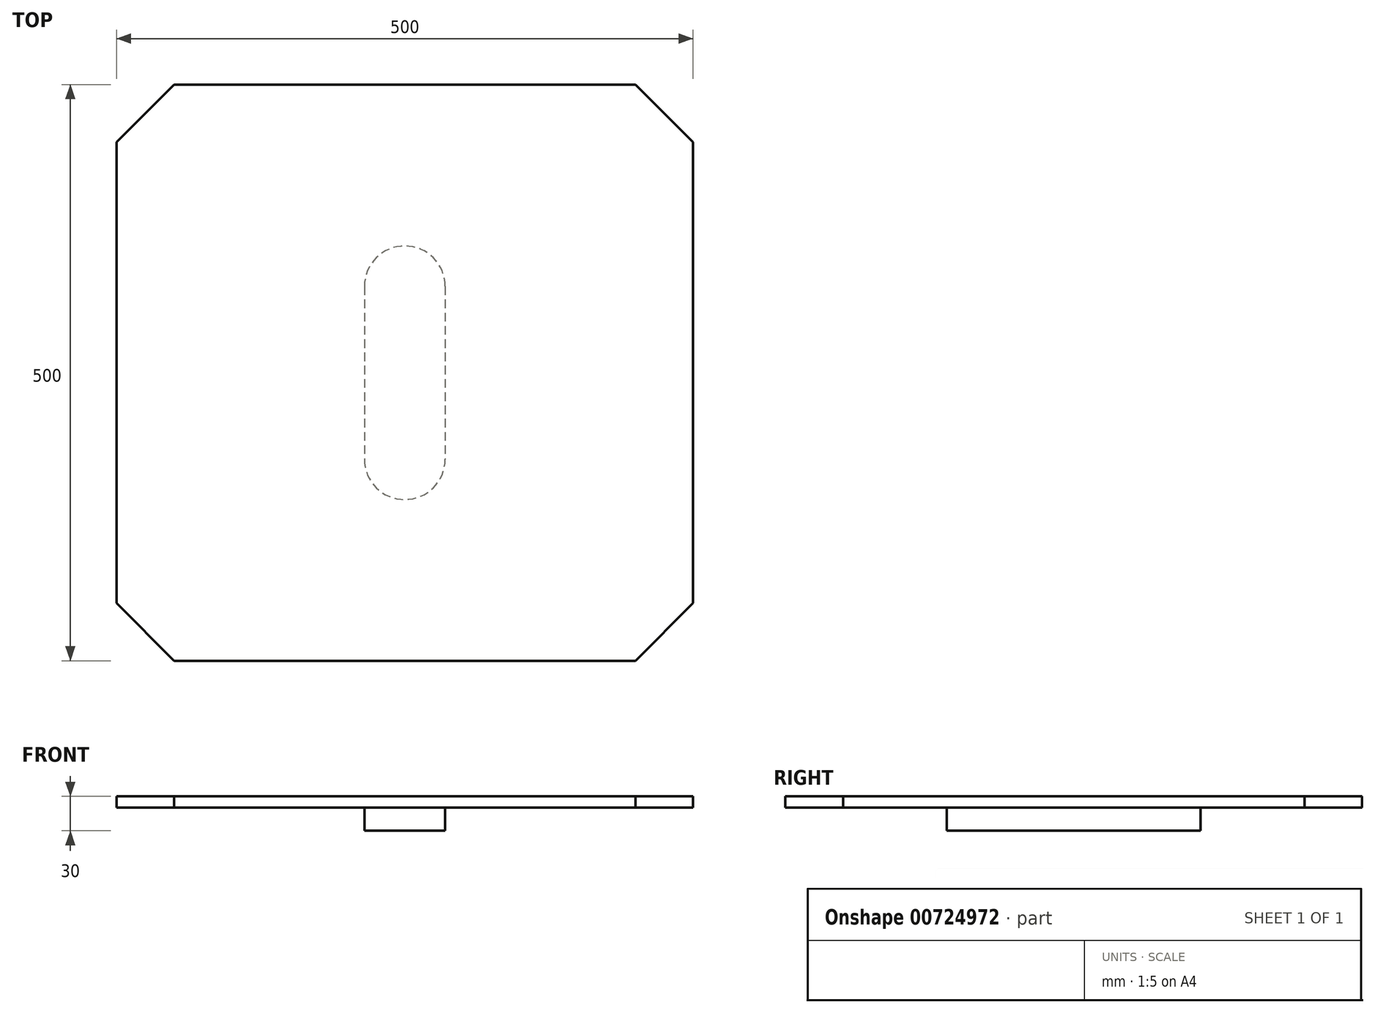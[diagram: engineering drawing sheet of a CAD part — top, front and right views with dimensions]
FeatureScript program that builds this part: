
annotation { "Feature Type Name" : "Feature", "Feature Type Description" : "" }
export const myFeature = defineFeature(function(context is Context, id is Id, definition is map)
    precondition{}
    {
        {
            var Q0;
            Q0=qCreatedBy(makeId("Top.planeOp"),FACE);
            var sketch = newSketch(context, id + "F0", { "sketchPlane" : qUnion([Q0])});
            skLineSegment(sketch, "E0.bottom", {"start": v(250, -250) * mm, "end": v(-250, -250) * mm});
            skLineSegment(sketch, "E0.top", {"start": v(250, 250) * mm, "end": v(-250, 250) * mm});
            skLineSegment(sketch, "E0.left", {"start": v(250, -250) * mm, "end": v(250, 250) * mm});
            skLineSegment(sketch, "E0.right", {"start": v(-250, -250) * mm, "end": v(-250, 250) * mm});
            skPoint(sketch, "E0.middle", {"position": v(0, 0) * mm});
            skSolve(sketch);
        }
        {
            var Q0;
            Q0=makeQuery(id+"F0.imprint","IMPRINT",FACE,{"disambiguationData":[TD([[makeQuery(id+"F0.imprint","IMPRINT",EDGE,{"derivedFrom":sQuery(id+"F0.wireOp",EDGE,"E0.bottom")}),-1.0]])]});
            extrude(context, id + "F1", {"entities" : qUnion([Q0]), "depth" : 30 * mm, "offsetDistance" : 25 * mm});
        }
        {
            var Q0;
            Q0=makeQuery(id+"F1.opExtrude","SWEPT_EDGE",EDGE,{"disambiguationData":[OSD([sQuery(id+"F0.wireOp",EDGE,"E0.bottom"),sQuery(id+"F0.wireOp",EDGE,"E0.left")])]});
            var Q1;
            Q1=makeQuery(id+"F1.opExtrude","SWEPT_EDGE",EDGE,{"disambiguationData":[OSD([sQuery(id+"F0.wireOp",EDGE,"E0.top"),sQuery(id+"F0.wireOp",EDGE,"E0.left")])]});
            var Q2;
            Q2=makeQuery(id+"F1.opExtrude","SWEPT_EDGE",EDGE,{"disambiguationData":[OSD([sQuery(id+"F0.wireOp",EDGE,"E0.bottom"),sQuery(id+"F0.wireOp",EDGE,"E0.right")])]});
            var Q3;
            Q3=makeQuery(id+"F1.opExtrude","SWEPT_EDGE",EDGE,{"disambiguationData":[OSD([sQuery(id+"F0.wireOp",EDGE,"E0.top"),sQuery(id+"F0.wireOp",EDGE,"E0.right")])]});
            chamfer(context, id + "F2", {"entities" : qUnion([Q0, Q1, Q2, Q3]), "width" : 50 * mm, "tangentPropagation" : true});
        }
        {
            var Q0;
            Q0=makeQuery(id+"F1.opExtrude","CAP_FACE",FACE,{"disambiguationData":[OSD([sQuery(id+"F0.wireOp",EDGE,"E0.bottom"),sQuery(id+"F0.wireOp",EDGE,"E0.top"),sQuery(id+"F0.wireOp",EDGE,"E0.left"),sQuery(id+"F0.wireOp",EDGE,"E0.right")])],"isStart":true});
            var sketch = newSketch(context, id + "F3", { "sketchPlane" : qUnion([Q0])});
            skLineSegment(sketch, "E1", {"start": v(0, -75) * mm, "end": v(0, 75) * mm, "construction": true});
            skArc(sketch, "E2.0.startCap", {"start": v(35, -75) * mm, "mid": v(0, -110) * mm, "end": v(-35, -75) * mm});
            skArc(sketch, "E2.0.endCap", {"start": v(-35, 75) * mm, "mid": v(0, 110) * mm, "end": v(35, 75) * mm});
            skLineSegment(sketch, "E2.0.left", {"start": v(-35, -75) * mm, "end": v(-35, 75) * mm});
            skLineSegment(sketch, "E2.0.right", {"start": v(35, -75) * mm, "end": v(35, 75) * mm});
            skSolve(sketch);
        }
        {
            var Q0;
            Q0=makeQuery(id+"F3.imprint","IMPRINT",FACE,{"disambiguationData":[TD([[makeQuery(id+"F3.imprint","IMPRINT",EDGE,{"derivedFrom":sQuery(id+"F3.wireOp",EDGE,"E2.0.startCap")}),-1.0]])]});
            extrude(context, id + "F4", {"entities" : qUnion([Q0]), "operationType" : NewBodyOperationType.REMOVE, "oppositeDirection" : true, "depth" : 20 * mm, "offsetDistance" : 25 * mm});
        }
    });
